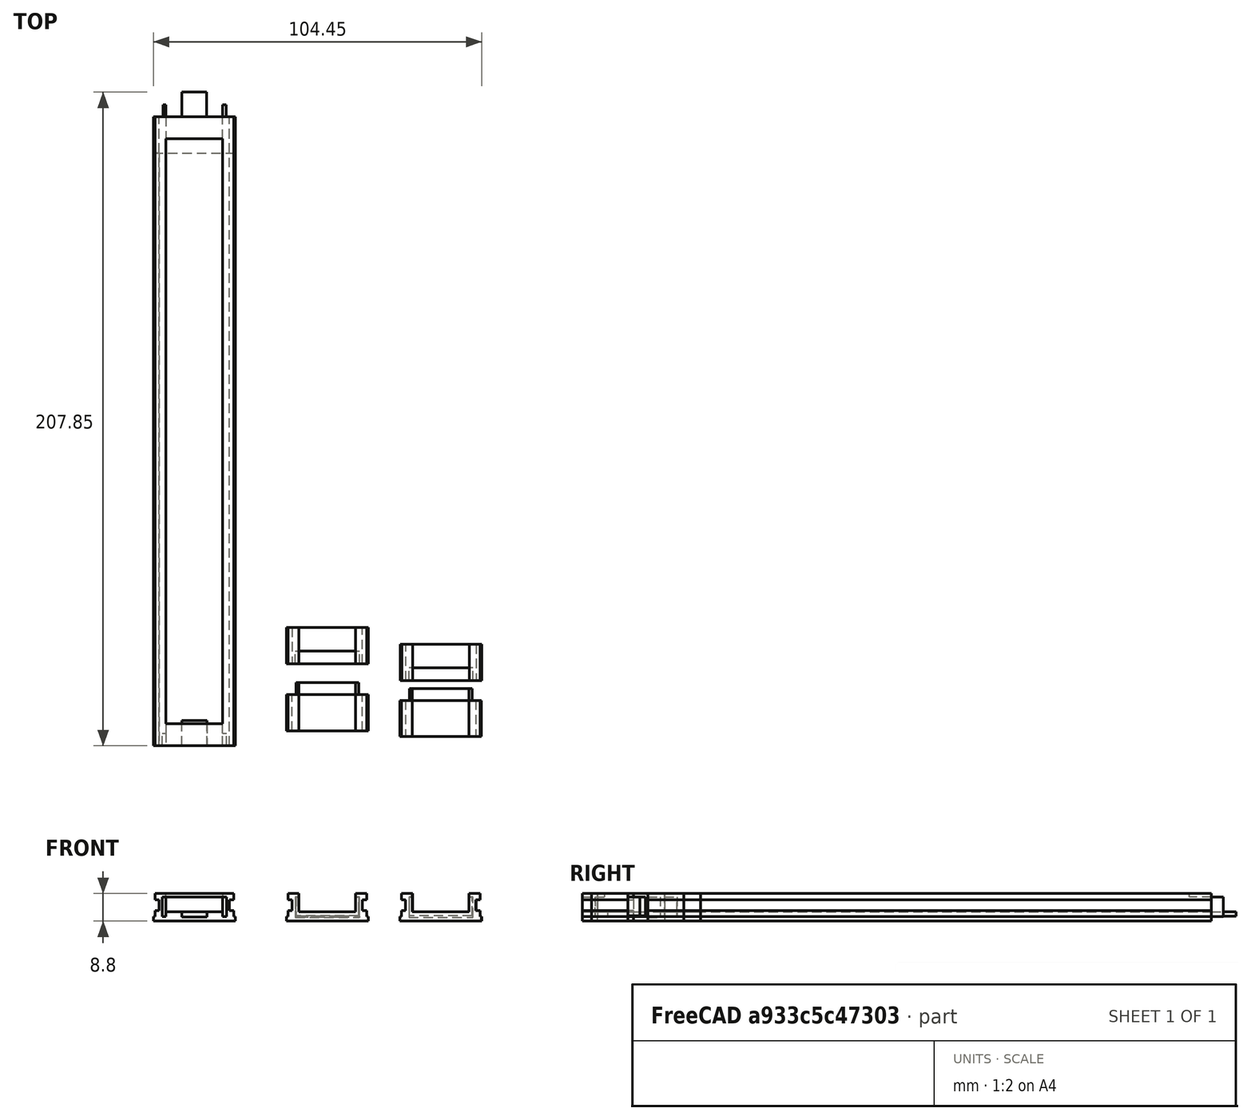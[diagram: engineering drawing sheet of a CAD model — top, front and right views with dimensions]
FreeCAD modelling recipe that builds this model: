
FCSTD DOCUMENT  (FreeCAD 0.18.3R)
Label: lamp.rail.template
License: All rights reserved
LicenseURL: http://en.wikipedia.org/wiki/All_rights_reserved
objects: Part::Extrusion×64, Part::Part2DObjectPython×46, Part::Cut×32, Part::Feature×26, Part::MultiFuse×13, Part::FeaturePython×3
note: 184 computed .brp shape members not serialized (recipe doc carries the construction recipe); baked Part::Feature solids carry a one-line shape summary decoded from their .brp

FEATURE [Part::Part2DObjectPython] Rectangle014  # Draft 2D object (typed FeaturePython)
  ChamferSize = 0
  Columns = 1
  FilletRadius = 0
  Height = 2
  Length = 24
  MakeFace = true
  Placement = pos=(-4.28928,0,-0.735044) rot=(1,0,0;1.5708rad)
  Rows = 1
FEATURE [Part::Part2DObjectPython] Rectangle013  # Draft 2D object (typed FeaturePython)
  ChamferSize = 0
  Columns = 1
  FilletRadius = 0
  Height = 2
  Length = 24
  MakeFace = true
  Placement = pos=(-4.28928,1.2e-15,4.66496) rot=(1,0,0;1.5708rad)
  Rows = 1
  Support = -> [Rectangle014]
FEATURE [Part::Part2DObjectPython] Rectangle015  # Draft 2D object (typed FeaturePython)
  ChamferSize = 0
  Columns = 1
  FilletRadius = 0
  Height = 7.5
  Length = 7.85
  MakeFace = true
  Placement = pos=(3.96072,7.85,0.865504) rot=(0,0,-1;1.5708rad)
  Rows = 1
FEATURE [Part::Part2DObjectPython] Rectangle016  # Draft 2D object (typed FeaturePython)
  ChamferSize = 0
  Columns = 1
  FilletRadius = 0
  Height = 5.79945
  Length = 13
  MakeFace = true
  Placement = pos=(14.2107,0,0.865504) rot=(0,0.707107,0.707107;3.14159rad)
  Rows = 1
FEATURE [Part::Part2DObjectPython] Rectangle017  # Draft 2D object (typed FeaturePython)
  ChamferSize = 0
  Columns = 1
  FilletRadius = 0
  Height = 3.4
  Length = 21.5
  MakeFace = true
  Placement = pos=(-3.03928,0,1.26496) rot=(1,0,0;1.5708rad)
  Rows = 1
  Support = -> [Rectangle013]
FEATURE [Part::Extrusion] Extrude026
  Base = -> Rectangle014
  Dir = (0,-1,2e-16)
  DirMode = 2
  FaceMakerClass = Part::FaceMakerBullseye
  LengthFwd = 23
  LengthRev = 0
  Solid = false
  Symmetric = false
FEATURE [Part::Extrusion] Extrude027
  Base = -> Rectangle016
  Dir = (0,1,-2e-16)
  DirMode = 2
  FaceMakerClass = Part::FaceMakerBullseye
  LengthFwd = -23
  LengthRev = 0
  Solid = false
  Symmetric = false
FEATURE [Part::Extrusion] Extrude028
  Base = -> Rectangle017
  Dir = (0,-1,2e-16)
  DirMode = 2
  FaceMakerClass = Part::FaceMakerBullseye
  LengthFwd = 23
  LengthRev = 0
  Solid = false
  Symmetric = false
FEATURE [Part::Extrusion] Extrude029
  Base = -> Rectangle013
  Dir = (0,-1,2e-16)
  DirMode = 2
  FaceMakerClass = Part::FaceMakerBullseye
  LengthFwd = 23
  LengthRev = 0
  Solid = false
  Symmetric = false
FEATURE [Part::Part2DObjectPython] Rectangle018  # Draft 2D object (typed FeaturePython)
  ChamferSize = 0
  Columns = 1
  FilletRadius = 0
  Height = 1.39945
  Length = 25
  MakeFace = true
  Placement = pos=(20.2107,-1e-15,-2.1345) rot=(0,0.707107,0.707107;3.14159rad)
  Rows = 1
FEATURE [Part::Extrusion] Extrude025
  Base = -> Rectangle018
  Dir = (0,1,-2e-16)
  DirMode = 2
  FaceMakerClass = Part::FaceMakerBullseye
  LengthFwd = -23
  LengthRev = 0
  Solid = false
  Symmetric = false
FEATURE [Part::MultiFuse] Fusion003
  Shapes = -> [Extrude029,Extrude028,Extrude026,Extrude025]
FEATURE [Part::Cut] Cut008
  Base = -> Fusion003
  Tool = -> Extrude027
FEATURE [Part::Part2DObjectPython] Rectangle020  # Draft 2D object (typed FeaturePython)
  ChamferSize = 0
  Columns = 1
  FilletRadius = 0
  Height = 2.5
  Length = 8
  MakeFace = true
  Placement = pos=(3.71072,-23,-1.6345) rot=(1,0,0;1.5708rad)
  Rows = 1
  Support = -> [Cut008]
FEATURE [Part::Extrusion] Extrude030
  Base = -> Rectangle020
  Dir = (-1e-16,-1,2e-16)
  DirMode = 2
  FaceMakerClass = Part::FaceMakerBullseye
  LengthFwd = -8
  LengthRev = 0
  Solid = false
  Symmetric = false
FEATURE [Part::Cut] Cut009
  Base = -> Cut008
  Tool = -> Extrude030
FEATURE [Part::Extrusion] Extrude031
  Base = -> Rectangle015
  Dir = (0,2e-16,1)
  DirMode = 2
  FaceMakerClass = Part::FaceMakerBullseye
  LengthFwd = -2
  LengthRev = 0
  Solid = false
  Symmetric = false
FEATURE [Part::MultiFuse] Fusion002
  Shapes = -> [Cut009,Extrude031]
FEATURE [Part::Part2DObjectPython] Rectangle019  # Draft 2D object (typed FeaturePython)
  ChamferSize = 0
  Columns = 1
  FilletRadius = 0
  Height = 23
  Length = 15
  MakeFace = true
  Placement = pos=(15.2107,0,6.66496) rot=(0,0,1;3.14159rad)
  Rows = 1
  Support = -> [Fusion002]
FEATURE [Part::Extrusion] Extrude024
  Base = -> Rectangle019
  Dir = (0,2e-16,1)
  DirMode = 2
  FaceMakerClass = Part::FaceMakerBullseye
  LengthFwd = -5.8
  LengthRev = 0
  Solid = false
  Symmetric = false
FEATURE [Part::Cut] Cut010
  Base = -> Fusion002
  Placement = pos=(1.15935,45.2064,-9.8e-15) rot=(0,0,1;0rad)
  Tool = -> Extrude024
FEATURE [Part::Part2DObjectPython] Rectangle021  # Draft 2D object (typed FeaturePython)
  ChamferSize = 0
  Columns = 1
  FilletRadius = 0
  Height = 32.5147
  Length = 55.6938
  MakeFace = true
  Placement = pos=(36.717,33.7064,-13.163) rot=(0,0.707107,0.707107;3.14159rad)
  Rows = 1
  Support = -> [Cut010]
FEATURE [Part::FeaturePython] Slice  # WARN: FeaturePython — macro-defined, semantics opaque (R4)
  Base = -> Cut010
  Mode = 1
  Tolerance = 0
  Tools = -> [Rectangle021]
FEATURE [Part::FeaturePython] Slice_child0  label="Slice.0"  # WARN: FeaturePython — macro-defined, semantics opaque (R4)
  Base = -> Slice
  FilterType = 1
  Invert = false
  OverrideMaxVal = 0
  Placement = pos=(-30.6082,-11.7295,9e-16) rot=(0,0,1;0rad)
  WindowFrom = 80
  WindowTo = 100
  items = 0
FEATURE [Part::FeaturePython] Slice_child1  label="Slice.1"  # WARN: FeaturePython — macro-defined, semantics opaque (R4)
  Base = -> Slice
  FilterType = 1
  Invert = false
  OverrideMaxVal = 0
  WindowFrom = 80
  WindowTo = 100
  items = 1
FEATURE [Part::Feature] Face
  Placement = pos=(-29.4488,33.4769,-8.9e-15) rot=(0,0,1;0rad)
  shape: bbox 2e-07 x 7.85 x 2 mm, 1 faces, 0 solids (baked)
FEATURE [Part::Extrusion] Extrusion
  Base = -> Face
  Dir = (0.2,0,0)
  DirMode = 0
  FaceMakerClass = Part::FaceMakerBullseye
  LengthFwd = 0
  LengthRev = 0
  Solid = true
  Symmetric = false
FEATURE [Part::Feature] Face001
  Placement = pos=(-29.4488,33.4769,-8.9e-15) rot=(0,0,1;0rad)
  shape: bbox 2e-07 x 7.85 x 2 mm, 1 faces, 0 solids (baked)
FEATURE [Part::Extrusion] Extrusion001
  Base = -> Face001
  Dir = (-0.2,0,0)
  DirMode = 0
  FaceMakerClass = Part::FaceMakerBullseye
  LengthFwd = 0
  LengthRev = 0
  Solid = true
  Symmetric = false
FEATURE [Part::MultiFuse] Fusion004
  Shapes = -> [Extrusion,Extrusion001,Slice_child0]
FEATURE [Part::Part2DObjectPython] Rectangle024  # Draft 2D object (typed FeaturePython)
  ChamferSize = 0
  Columns = 1
  FilletRadius = 0
  Height = 17
  Length = 11.5
  MakeFace = true
  Placement = pos=(-30.2381,33.4769,0.864956) rot=(0,0,-1;1.5708rad)
  Rows = 1
  Support = -> [Slice_child1]
FEATURE [Part::Extrusion] Extrude032
  Base = -> Rectangle024
  Dir = (0,2e-16,1)
  DirMode = 2
  FaceMakerClass = Part::FaceMakerBullseye
  LengthFwd = 10
  LengthRev = 0
  Solid = false
  Symmetric = false
FEATURE [Part::Cut] Cut011
  Base = -> Fusion004
  Tool = -> Extrude032
FEATURE [Part::Part2DObjectPython] Rectangle025  # Draft 2D object (typed FeaturePython)
  ChamferSize = 0
  Columns = 1
  FilletRadius = 0
  Height = 17
  Length = 11.5
  MakeFace = true
  Placement = pos=(0.370074,33.7064,0.864956) rot=(0,0,-1;1.5708rad)
  Rows = 1
FEATURE [Part::Extrusion] Extrude033
  Base = -> Rectangle025
  Dir = (0,2e-16,1)
  DirMode = 2
  FaceMakerClass = Part::FaceMakerBullseye
  LengthFwd = 10
  LengthRev = 0
  Solid = false
  Symmetric = false
FEATURE [Part::Cut] Cut012
  Base = -> Slice_child1
  Tool = -> Extrude033
FEATURE [Part::Part2DObjectPython] Rectangle027  # Draft 2D object (typed FeaturePython)
  ChamferSize = 0
  Columns = 1
  FilletRadius = 0
  Height = 3.8
  Length = 8
  MakeFace = true
  Placement = pos=(4.87007,22.2064,-1.6345) rot=(0,0,1;0rad)
  Rows = 1
  Support = -> [Cut012]
FEATURE [Part::Part2DObjectPython] Rectangle028  # Draft 2D object (typed FeaturePython)
  ChamferSize = 0
  Columns = 1
  FilletRadius = 0
  Height = 4
  Length = 7.9
  MakeFace = true
  Placement = pos=(-25.6881,33.4769,-1.1345) rot=(0,0,1;0rad)
  Rows = 1
FEATURE [Part::Extrusion] Extrude040
  Base = -> Rectangle028
  Dir = (0,2e-16,1)
  DirMode = 2
  FaceMakerClass = Part::FaceMakerBullseye
  LengthFwd = 0.6
  LengthRev = 0
  Solid = false
  Symmetric = false
FEATURE [Part::Cut] Cut018
  Base = -> Cut011
  Tool = -> Extrude040
FEATURE [Part::Extrusion] Extrude041
  Base = -> Rectangle027
  Dir = (0,2e-16,1)
  DirMode = 2
  FaceMakerClass = Part::FaceMakerBullseye
  LengthFwd = 0.9
  LengthRev = 0
  Solid = false
  Symmetric = false
FEATURE [Part::MultiFuse] Fusion005
  Shapes = -> [Cut012,Extrude041]
FEATURE [Part::Part2DObjectPython] Rectangle029  # Draft 2D object (typed FeaturePython)
  ChamferSize = 0
  Columns = 1
  FilletRadius = 0
  Height = 3.85
  Length = 7.9
  MakeFace = true
  Placement = pos=(-17.7881,37.4769,-1.1345) rot=(0,1,0;3.14159rad)
  Rows = 1
  Support = -> [Cut018]
FEATURE [Part::Extrusion] Extrude042
  Base = -> Rectangle029
  Dir = (0,0,-1)
  DirMode = 2
  FaceMakerClass = Part::FaceMakerBullseye
  LengthFwd = 0.1
  LengthRev = 0
  Solid = false
  Symmetric = false
FEATURE [Part::MultiFuse] Fusion006
  Shapes = -> [Cut018,Extrude042]
FEATURE [Part::Part2DObjectPython] Rectangle030  # Draft 2D object (typed FeaturePython)
  ChamferSize = 0
  Columns = 1
  FilletRadius = 0
  Height = 6.3
  Length = 1.1
  MakeFace = true
  Placement = pos=(-12.1381,33.4769,-0.735044) rot=(0,0.707107,0.707107;3.14159rad)
  Rows = 1
  Support = -> [Fusion006]
FEATURE [Part::Part2DObjectPython] Rectangle031  # Draft 2D object (typed FeaturePython)
  ChamferSize = 0
  Columns = 1
  FilletRadius = 0
  Height = 6.3
  Length = 1
  MakeFace = true
  Placement = pos=(-30.2381,33.4769,-0.735044) rot=(0,0.707107,0.707107;3.14159rad)
  Rows = 1
FEATURE [Part::Part2DObjectPython] Rectangle032  # Draft 2D object (typed FeaturePython)
  ChamferSize = 0
  Columns = 1
  FilletRadius = 0
  Height = 6.3
  Length = 1.2
  MakeFace = true
  Placement = pos=(-0.829926,22.2064,-0.735044) rot=(1,0,0;1.5708rad)
  Rows = 1
  Support = -> [Fusion005]
FEATURE [Part::Part2DObjectPython] Rectangle033  # Draft 2D object (typed FeaturePython)
  ChamferSize = 0
  Columns = 1
  FilletRadius = 0
  Height = 6.3
  Length = 1.2
  MakeFace = true
  Placement = pos=(17.3701,22.2064,-0.735044) rot=(1,0,0;1.5708rad)
  Rows = 1
FEATURE [Part::Extrusion] Extrude045
  Base = -> Rectangle032
  Dir = (2.69e-14,-1,2e-16)
  DirMode = 2
  FaceMakerClass = Part::FaceMakerBullseye
  LengthFwd = -4
  LengthRev = 0
  Placement = pos=(-0.5,-1.14e-13,0) rot=(0,0,1;0rad)
  Solid = false
  Symmetric = false
FEATURE [Part::Extrusion] Extrude046
  Base = -> Rectangle033
  Dir = (2.69e-14,-1,2e-16)
  DirMode = 2
  FaceMakerClass = Part::FaceMakerBullseye
  LengthFwd = -4
  LengthRev = 0
  Placement = pos=(0.5,1.101e-13,0) rot=(0,0,1;0rad)
  Solid = false
  Symmetric = false
FEATURE [Part::Extrusion] Extrude047
  Base = -> Rectangle030
  Dir = (-2.5e-14,1,-2e-16)
  DirMode = 2
  FaceMakerClass = Part::FaceMakerBullseye
  LengthFwd = 3.8
  LengthRev = 0
  Solid = false
  Symmetric = false
FEATURE [Part::Extrusion] Extrude048
  Base = -> Rectangle031
  Dir = (-2.5e-14,1,-2e-16)
  DirMode = 2
  FaceMakerClass = Part::FaceMakerBullseye
  LengthFwd = 3.8
  LengthRev = 0
  Solid = false
  Symmetric = false
FEATURE [Part::Part2DObjectPython] Rectangle034  # Draft 2D object (typed FeaturePython)
  ChamferSize = 0
  Columns = 1
  FilletRadius = 0
  Height = 3.8
  Length = 1.1
  MakeFace = true
  Placement = pos=(-12.1381,33.4769,-0.735044) rot=(0,1,0;3.14159rad)
  Rows = 1
  Support = -> [Extrude047]
FEATURE [Part::Extrusion] Extrude049
  Base = -> Rectangle034
  Dir = (2.55e-14,-2e-16,-1)
  DirMode = 2
  FaceMakerClass = Part::FaceMakerBullseye
  LengthFwd = -0.1
  LengthRev = 0
  Solid = false
  Symmetric = false
FEATURE [Part::Cut] Cut021
  Base = -> Extrude047
  Placement = pos=(0.5,2.27e-13,0) rot=(0,0,1;0rad)
  Tool = -> Extrude049
FEATURE [Part::Part2DObjectPython] Rectangle035  # Draft 2D object (typed FeaturePython)
  ChamferSize = 0
  Columns = 1
  FilletRadius = 0
  Height = 3.8
  Length = 1
  MakeFace = true
  Placement = pos=(-30.2381,33.4769,-0.735044) rot=(0,1,0;3.14159rad)
  Rows = 1
  Support = -> [Fusion006]
FEATURE [Part::Extrusion] Extrude050
  Base = -> Rectangle035
  Dir = (2.55e-14,-2e-16,-1)
  DirMode = 2
  FaceMakerClass = Part::FaceMakerBullseye
  LengthFwd = -0.1
  LengthRev = 0
  Solid = false
  Symmetric = false
FEATURE [Part::Cut] Cut022
  Base = -> Extrude048
  Placement = pos=(-0.5,-7.1e-15,0) rot=(0,0,1;0rad)
  Tool = -> Extrude050
FEATURE [Part::Part2DObjectPython] Rectangle036  # Draft 2D object (typed FeaturePython)
  ChamferSize = 0
  Columns = 1
  FilletRadius = 0
  Height = 3.85
  Length = 7.9
  MakeFace = true
  Placement = pos=(-17.7881,37.4769,-1.2345) rot=(0,1,0;3.14159rad)
  Rows = 1
FEATURE [Part::Extrusion] Extrude051
  Base = -> Rectangle036
  Dir = (0,0,-1)
  DirMode = 2
  FaceMakerClass = Part::FaceMakerBullseye
  LengthFwd = 0.1
  LengthRev = 0
  Solid = false
  Symmetric = false
FEATURE [Part::Part2DObjectPython] Rectangle037  # Draft 2D object (typed FeaturePython)
  ChamferSize = 0
  Columns = 1
  FilletRadius = 0
  Height = 7.9
  Length = 4.1
  MakeFace = true
  Placement = pos=(-25.6881,33.4769,-0.534496) rot=(0.707107,0.707107,0;3.14159rad)
  Rows = 1
FEATURE [Part::Extrusion] Extrude052
  Base = -> Rectangle037
  Dir = (0,-3e-16,-1)
  DirMode = 2
  FaceMakerClass = Part::FaceMakerBullseye
  LengthFwd = 1
  LengthRev = 0
  Solid = false
  Symmetric = false
FEATURE [Part::Part2DObjectPython] Rectangle038  # Draft 2D object (typed FeaturePython)
  ChamferSize = 0
  Columns = 1
  FilletRadius = 0
  Height = 3.8
  Length = 8
  MakeFace = true
  Placement = pos=(4.87007,22.2064,-0.734496) rot=(0,0,1;0rad)
  Rows = 1
FEATURE [Part::Extrusion] Extrude053
  Base = -> Rectangle038
  Dir = (0,2e-16,1)
  DirMode = 2
  FaceMakerClass = Part::FaceMakerBullseye
  LengthFwd = -0.1
  LengthRev = 0
  Solid = false
  Symmetric = false
FEATURE [Part::Part2DObjectPython] Rectangle039  # Draft 2D object (typed FeaturePython)
  ChamferSize = 0
  Columns = 1
  FilletRadius = 0
  Height = 2
  Length = 11.5
  MakeFace = true
  Placement = pos=(-33.7381,33.4769,4.66496) rot=(0.57735,-0.57735,-0.57735;2.0944rad)
  Rows = 1
FEATURE [Part::Extrusion] Extrude054
  Base = -> Rectangle039
  Dir = (-1,-2e-16,-2e-16)
  DirMode = 2
  FaceMakerClass = Part::FaceMakerBullseye
  LengthFwd = 0.5
  LengthRev = 0
  Solid = false
  Symmetric = false
FEATURE [Part::Part2DObjectPython] Rectangle040  # Draft 2D object (typed FeaturePython)
  ChamferSize = 0
  Columns = 1
  FilletRadius = 0
  Height = 2
  Length = 11.5
  MakeFace = true
  Placement = pos=(-33.7381,33.4769,-0.735044) rot=(0.57735,-0.57735,-0.57735;2.0944rad)
  Rows = 1
FEATURE [Part::Extrusion] Extrude055
  Base = -> Rectangle040
  Dir = (-1,-2e-16,-2e-16)
  DirMode = 2
  FaceMakerClass = Part::FaceMakerBullseye
  LengthFwd = 0.5
  LengthRev = 0
  Solid = false
  Symmetric = false
FEATURE [Part::Part2DObjectPython] Rectangle041  # Draft 2D object (typed FeaturePython)
  ChamferSize = 0
  Columns = 1
  FilletRadius = 0
  Height = 1.39945
  Length = 11.5
  MakeFace = true
  Placement = pos=(-34.2381,33.4769,-2.1345) rot=(0.57735,-0.57735,-0.57735;2.0944rad)
  Rows = 1
FEATURE [Part::Extrusion] Extrude056
  Base = -> Rectangle041
  Dir = (-1,-2e-16,-2e-16)
  DirMode = 2
  FaceMakerClass = Part::FaceMakerBullseye
  LengthFwd = 0.5
  LengthRev = 0
  Solid = false
  Symmetric = false
FEATURE [Part::Part2DObjectPython] Rectangle042  # Draft 2D object (typed FeaturePython)
  ChamferSize = 0
  Columns = 1
  FilletRadius = 0
  Height = 3.4
  Length = 11.5
  MakeFace = true
  Placement = pos=(-32.4881,33.4769,1.26496) rot=(0.57735,-0.57735,-0.57735;2.0944rad)
  Rows = 1
FEATURE [Part::Extrusion] Extrude057
  Base = -> Rectangle042
  Dir = (-1,-2e-16,-2e-16)
  DirMode = 2
  FaceMakerClass = Part::FaceMakerBullseye
  LengthFwd = 0.4
  LengthRev = 0
  Solid = false
  Symmetric = false
FEATURE [Part::Part2DObjectPython] Rectangle043  # Draft 2D object (typed FeaturePython)
  ChamferSize = 0
  Columns = 1
  FilletRadius = 0
  Height = 3.4
  Length = 11.5
  MakeFace = true
  Placement = pos=(-10.9881,33.4769,1.26496) rot=(0.57735,-0.57735,-0.57735;2.0944rad)
  Rows = 1
FEATURE [Part::Extrusion] Extrude058
  Base = -> Rectangle043
  Dir = (-1,-2e-16,-2e-16)
  DirMode = 2
  FaceMakerClass = Part::FaceMakerBullseye
  LengthFwd = -0.4
  LengthRev = 0
  Solid = false
  Symmetric = false
FEATURE [Part::Part2DObjectPython] Rectangle044  # Draft 2D object (typed FeaturePython)
  ChamferSize = 0
  Columns = 1
  FilletRadius = 0
  Height = 2
  Length = 11.5
  MakeFace = true
  Placement = pos=(-9.73812,33.4769,4.66496) rot=(0.57735,-0.57735,-0.57735;2.0944rad)
  Rows = 1
FEATURE [Part::Part2DObjectPython] Rectangle045  # Draft 2D object (typed FeaturePython)
  ChamferSize = 0
  Columns = 1
  FilletRadius = 0
  Height = 2
  Length = 11.5
  MakeFace = true
  Placement = pos=(-9.73812,33.4769,-0.735044) rot=(0.57735,-0.57735,-0.57735;2.0944rad)
  Rows = 1
FEATURE [Part::Part2DObjectPython] Rectangle046  # Draft 2D object (typed FeaturePython)
  ChamferSize = 0
  Columns = 1
  FilletRadius = 0
  Height = 1.39945
  Length = 11.5
  MakeFace = true
  Placement = pos=(-9.23812,33.4769,-2.1345) rot=(0.57735,-0.57735,-0.57735;2.0944rad)
  Rows = 1
FEATURE [Part::Extrusion] Extrude059
  Base = -> Rectangle044
  Dir = (-1,-2e-16,-2e-16)
  DirMode = 2
  FaceMakerClass = Part::FaceMakerBullseye
  LengthFwd = -0.5
  LengthRev = 0
  Solid = false
  Symmetric = false
FEATURE [Part::Extrusion] Extrude060
  Base = -> Rectangle045
  Dir = (-1,-2e-16,-2e-16)
  DirMode = 2
  FaceMakerClass = Part::FaceMakerBullseye
  LengthFwd = -0.5
  LengthRev = 0
  Solid = false
  Symmetric = false
FEATURE [Part::Extrusion] Extrude061
  Base = -> Rectangle046
  Dir = (-1,-2e-16,-2e-16)
  DirMode = 2
  FaceMakerClass = Part::FaceMakerBullseye
  LengthFwd = -0.5
  LengthRev = 0
  Solid = false
  Symmetric = false
FEATURE [Part::Part2DObjectPython] Rectangle047  # Draft 2D object (typed FeaturePython)
  ChamferSize = 0
  Columns = 1
  FilletRadius = 0
  Height = 11.5
  Length = 18
  MakeFace = true
  Placement = pos=(-30.7381,21.9769,0.864956) rot=(0,0,1;0rad)
  Rows = 1
FEATURE [Part::Extrusion] Extrude062
  Base = -> Rectangle047
  Dir = (0,0,1)
  DirMode = 2
  FaceMakerClass = Part::FaceMakerBullseye
  LengthFwd = 10
  LengthRev = 0
  Solid = false
  Symmetric = false
FEATURE [Part::Cut] Cut025
  Base = -> Fusion006
  Tool = -> Extrude062
FEATURE [Part::MultiFuse] Fusion007
  Shapes = -> [Extrude051,Cut025]
FEATURE [Part::Cut] Cut026
  Base = -> Fusion007
  Tool = -> Extrude052
FEATURE [Part::MultiFuse] Fusion008
  Shapes = -> [Cut026,Extrude061,Extrude060,Extrude058,Extrude059,Extrude056,Extrude055,Extrude057,Extrude054]
FEATURE [Part::Part2DObjectPython] Rectangle048  # Draft 2D object (typed FeaturePython)
  ChamferSize = 0
  Columns = 1
  FilletRadius = 0
  Height = 2
  Length = 11.5
  MakeFace = true
  Placement = pos=(20.8701,33.7064,6.66496) rot=(0.57735,-0.57735,0.57735;4.18879rad)
  Rows = 1
FEATURE [Part::Part2DObjectPython] Rectangle049  # Draft 2D object (typed FeaturePython)
  ChamferSize = 0
  Columns = 1
  FilletRadius = 0
  Height = 2
  Length = 11.5
  MakeFace = true
  Placement = pos=(20.8701,33.7064,1.26496) rot=(0.57735,-0.57735,0.57735;4.18879rad)
  Rows = 1
FEATURE [Part::Part2DObjectPython] Rectangle050  # Draft 2D object (typed FeaturePython)
  ChamferSize = 0
  Columns = 1
  FilletRadius = 0
  Height = 1.39945
  Length = 11.5
  MakeFace = true
  Placement = pos=(21.3701,33.7064,-0.735044) rot=(0.57735,-0.57735,0.57735;4.18879rad)
  Rows = 1
FEATURE [Part::Part2DObjectPython] Rectangle051  # Draft 2D object (typed FeaturePython)
  ChamferSize = 0
  Columns = 1
  FilletRadius = 0
  Height = 3.4
  Length = 11.5
  MakeFace = true
  Placement = pos=(19.6201,33.7064,4.66496) rot=(0.57735,-0.57735,0.57735;4.18879rad)
  Rows = 1
FEATURE [Part::Part2DObjectPython] Rectangle052  # Draft 2D object (typed FeaturePython)
  ChamferSize = 0
  Columns = 1
  FilletRadius = 0
  Height = 2
  Length = 11.5
  MakeFace = true
  Placement = pos=(-3.12993,33.7064,6.66496) rot=(0.57735,-0.57735,0.57735;4.18879rad)
  Rows = 1
FEATURE [Part::Part2DObjectPython] Rectangle053  # Draft 2D object (typed FeaturePython)
  ChamferSize = 0
  Columns = 1
  FilletRadius = 0
  Height = 3.4
  Length = 11.5
  MakeFace = true
  Placement = pos=(-1.87993,33.7064,4.66496) rot=(0.57735,-0.57735,0.57735;4.18879rad)
  Rows = 1
FEATURE [Part::Part2DObjectPython] Rectangle054  # Draft 2D object (typed FeaturePython)
  ChamferSize = 0
  Columns = 1
  FilletRadius = 0
  Height = 2
  Length = 11.5
  MakeFace = true
  Placement = pos=(-3.12993,33.7064,1.26496) rot=(0.57735,-0.57735,0.57735;4.18879rad)
  Rows = 1
FEATURE [Part::Part2DObjectPython] Rectangle055  # Draft 2D object (typed FeaturePython)
  ChamferSize = 0
  Columns = 1
  FilletRadius = 0
  Height = 1.39945
  Length = 11.5
  MakeFace = true
  Placement = pos=(-3.62993,33.7064,-0.735044) rot=(0.57735,-0.57735,0.57735;4.18879rad)
  Rows = 1
FEATURE [Part::Extrusion] Extrude063
  Base = -> Rectangle048
  Dir = (1,-1e-16,1e-16)
  DirMode = 2
  FaceMakerClass = Part::FaceMakerBullseye
  LengthFwd = 0.5
  LengthRev = 0
  Solid = false
  Symmetric = false
FEATURE [Part::Extrusion] Extrude064
  Base = -> Rectangle049
  Dir = (1,-1e-16,1e-16)
  DirMode = 2
  FaceMakerClass = Part::FaceMakerBullseye
  LengthFwd = 0.5
  LengthRev = 0
  Solid = false
  Symmetric = false
FEATURE [Part::Extrusion] Extrude065
  Base = -> Rectangle050
  Dir = (1,-1e-16,1e-16)
  DirMode = 2
  FaceMakerClass = Part::FaceMakerBullseye
  LengthFwd = 0.5
  LengthRev = 0
  Solid = false
  Symmetric = false
FEATURE [Part::Extrusion] Extrude066
  Base = -> Rectangle052
  Dir = (1,-1e-16,1e-16)
  DirMode = 2
  FaceMakerClass = Part::FaceMakerBullseye
  LengthFwd = -0.5
  LengthRev = 0
  Solid = false
  Symmetric = false
FEATURE [Part::Extrusion] Extrude067
  Base = -> Rectangle054
  Dir = (1,-1e-16,1e-16)
  DirMode = 2
  FaceMakerClass = Part::FaceMakerBullseye
  LengthFwd = -0.5
  LengthRev = 0
  Solid = false
  Symmetric = false
FEATURE [Part::Extrusion] Extrude068
  Base = -> Rectangle055
  Dir = (1,-1e-16,1e-16)
  DirMode = 2
  FaceMakerClass = Part::FaceMakerBullseye
  LengthFwd = -0.5
  LengthRev = 0
  Solid = false
  Symmetric = false
FEATURE [Part::Extrusion] Extrude069
  Base = -> Rectangle053
  Dir = (1,-1e-16,1e-16)
  DirMode = 2
  FaceMakerClass = Part::FaceMakerBullseye
  LengthFwd = -0.4
  LengthRev = 0
  Solid = false
  Symmetric = false
FEATURE [Part::Part2DObjectPython] Rectangle056  # Draft 2D object (typed FeaturePython)
  ChamferSize = 0
  Columns = 1
  FilletRadius = 0
  Height = 11.5
  Length = 18
  MakeFace = true
  Placement = pos=(-0.129926,22.2064,0.864956) rot=(0,0,1;0rad)
  Rows = 1
  Support = -> [Fusion005]
FEATURE [Part::Extrusion] Extrude070
  Base = -> Rectangle056
  Dir = (0,0,1)
  DirMode = 2
  FaceMakerClass = Part::FaceMakerBullseye
  LengthFwd = 10
  LengthRev = 0
  Solid = false
  Symmetric = false
FEATURE [Part::Cut] Cut027
  Base = -> Fusion005
  Tool = -> Extrude070
FEATURE [Part::Cut] Cut028
  Base = -> Cut027
  Tool = -> Extrude045
FEATURE [Part::Cut] Cut029
  Base = -> Cut028
  Tool = -> Extrude046
FEATURE [Part::Extrusion] Extrude071
  Base = -> Rectangle051
  Dir = (1,-1e-16,1e-16)
  DirMode = 2
  FaceMakerClass = Part::FaceMakerBullseye
  LengthFwd = 0.4
  LengthRev = 0
  Solid = false
  Symmetric = false
FEATURE [Part::MultiFuse] Fusion010
  Shapes = -> [Extrude063,Extrude064,Extrude065,Extrude066,Extrude067,Extrude068,Extrude069,Extrude071]
FEATURE [Part::Cut] Cut030
  Base = -> Cut029
  Tool = -> Extrude053
FEATURE [Part::MultiFuse] Fusion011
  Placement = pos=(-30.6082,21.1066,-8e-15) rot=(0,0,1;0rad)
  Shapes = -> [Cut030,Fusion010]
FEATURE [Part::MultiFuse] Fusion012
  Shapes = -> [Cut021,Cut022,Fusion008]
FEATURE [Part::Part2DObjectPython] Rectangle057  # Draft 2D object (typed FeaturePython)
  ChamferSize = 0
  Columns = 1
  FilletRadius = 0
  Height = 3.75
  Length = 7.9
  MakeFace = true
  Placement = pos=(-25.6881,41.3269,-1.3345) rot=(1,0,0;3.14159rad)
  Rows = 1
  Support = -> [Fusion012]
FEATURE [Part::Extrusion] Extrude072
  Base = -> Rectangle057
  Dir = (0,-1e-16,-1)
  DirMode = 2
  FaceMakerClass = Part::FaceMakerBullseye
  LengthFwd = -0.8
  LengthRev = 0
  Solid = false
  Symmetric = false
FEATURE [Part::Cut] Cut031
  Base = -> Fusion012
  Tool = -> Extrude072
FEATURE [Part::Feature] Face002
  Placement = pos=(-30.6082,21.1066,-8e-15) rot=(0,0,1;0rad)
  shape: bbox 8 x 4.2 x 3e-07 mm, 1 faces, 0 solids (baked)
FEATURE [Part::Extrusion] Extrusion002
  Base = -> Face002
  Dir = (0,2e-16,0.8)
  DirMode = 0
  FaceMakerClass = Part::FaceMakerBullseye
  LengthFwd = 0
  LengthRev = 0
  Solid = true
  Symmetric = false
FEATURE [Part::MultiFuse] Fusion
  Shapes = -> [Extrusion002,Fusion011]
FEATURE [Part::Feature] Fusion013005001  label="Fusion013006"
  shape: bbox 26 x 207.9 x 8.8 mm, 55 faces (baked)
FEATURE [Part::Feature] Face003
  Placement = pos=(-30.6082,21.1066,-8e-15) rot=(0,0,1;0rad)
  shape: bbox 5 x 5.243e-07 x 1.6 mm, 1 faces, 0 solids (baked)
FEATURE [Part::Extrusion] Extrusion003
  Base = -> Face003
  Dir = (0,4,0)
  DirMode = 0
  FaceMakerClass = Part::FaceMakerBullseye
  LengthFwd = 0
  LengthRev = 0
  Solid = true
  Symmetric = false
FEATURE [Part::Cut] Cut
  Base = -> Fusion
  Tool = -> Extrusion003
FEATURE [Part::Feature] Face004
  Placement = pos=(-30.6082,21.1066,-8e-15) rot=(0,0,1;0rad)
  shape: bbox 5 x 5.243e-07 x 1.6 mm, 1 faces, 0 solids (baked)
FEATURE [Part::Feature] Face005
  shape: bbox 8 x 5.243e-07 x 1.699 mm, 1 faces, 0 solids (baked)
FEATURE [Part::Extrusion] Extrusion004
  Base = -> Face004
  Dir = (0,4,0)
  DirMode = 0
  FaceMakerClass = Part::FaceMakerBullseye
  LengthFwd = 0
  LengthRev = 0
  Solid = true
  Symmetric = false
FEATURE [Part::Cut] Cut032
  Base = -> Cut
  Tool = -> Extrusion004
FEATURE [Part::Extrusion] Extrusion005
  Base = -> Face005
  Dir = (0,-4,0)
  DirMode = 0
  FaceMakerClass = Part::FaceMakerBullseye
  LengthFwd = 0
  LengthRev = 0
  Solid = true
  Symmetric = false
FEATURE [Part::Feature] Face006
  shape: bbox 5 x 4 x 5.243e-07 mm, 1 faces, 0 solids (baked)
FEATURE [Part::Extrusion] Extrusion006
  Base = -> Face006
  Dir = (0,0,-0.0994518)
  DirMode = 0
  FaceMakerClass = Part::FaceMakerBullseye
  LengthFwd = 0
  LengthRev = 0
  Solid = true
  Symmetric = false
FEATURE [Part::Feature] Face007
  shape: bbox 5 x 4 x 5.243e-07 mm, 1 faces, 0 solids (baked)
FEATURE [Part::Extrusion] Extrusion007
  Base = -> Face007
  Dir = (0,0,-0.0994518)
  DirMode = 0
  FaceMakerClass = Part::FaceMakerBullseye
  LengthFwd = 0
  LengthRev = 0
  Solid = true
  Symmetric = false
FEATURE [Part::Feature] Face008
  shape: bbox 1.2 x 4 x 5.243e-07 mm, 1 faces, 0 solids (baked)
FEATURE [Part::Extrusion] Extrusion008
  Base = -> Face008
  Dir = (2.7e-15,0,-0.0994518)
  DirMode = 0
  FaceMakerClass = Part::FaceMakerBullseye
  LengthFwd = 0
  LengthRev = 0
  Solid = true
  Symmetric = false
FEATURE [Part::Feature] Face009
  shape: bbox 1.2 x 4 x 5.243e-07 mm, 1 faces, 0 solids (baked)
FEATURE [Part::Extrusion] Extrusion009
  Base = -> Face009
  Dir = (2.7e-15,0,-0.0994518)
  DirMode = 0
  FaceMakerClass = Part::FaceMakerBullseye
  LengthFwd = 0
  LengthRev = 0
  Solid = true
  Symmetric = false
FEATURE [Part::Cut] Cut033
  Base = -> Cut032
  Tool = -> Extrusion009
FEATURE [Part::Cut] Cut034
  Base = -> Cut033
  Tool = -> Extrusion008
FEATURE [Part::Cut] Cut035
  Base = -> Cut034
  Tool = -> Extrusion007
FEATURE [Part::Cut] Cut036
  Base = -> Cut035
  Tool = -> Extrusion006
FEATURE [Part::MultiFuse] Fusion013005002
  Shapes = -> [Extrusion005,Cut036]
FEATURE [Part::Feature] Fusion013005002001  label="Fusion013005003"
  shape: bbox 26 x 11.5 x 8.799 mm, 28 faces (baked)
FEATURE [Part::Part2DObjectPython] Rectangle  # Draft 2D object (typed FeaturePython)
  ChamferSize = 0
  Columns = 1
  FilletRadius = 0
  Height = 4
  Length = 20.4
  MakeFace = true
  Placement = pos=(-31.9381,43.313,-0.834496) rot=(0,0,1;0rad)
  Rows = 1
FEATURE [Part::Extrusion] Extrude
  Base = -> Rectangle
  Dir = (-7.3e-15,3e-16,1)
  DirMode = 2
  FaceMakerClass = Part::FaceMakerBullseye
  LengthFwd = -0.1
  LengthRev = 0
  Solid = false
  Symmetric = false
FEATURE [Part::Cut] Cut037
  Base = -> Fusion013005002001
  Tool = -> Extrude
FEATURE [Part::Feature] Cut037_solid  label="Cut037 (Solid)"
  shape: bbox 26 x 11.5 x 8.799 mm, 31 faces (baked)
FEATURE [Part::Feature] Cut037_solid001  label="Cut037 (Solid)001"
  shape: bbox 26 x 11.5 x 8.799 mm, 28 faces (baked)
FEATURE [Part::Feature] Cut037_solid001001  label="Cut037 (Solid)002"
  Placement = pos=(36.1596,-5.32723,-2.2e-15) rot=(0,0,1;0rad)
  shape: bbox 26 x 11.5 x 8.799 mm, 28 faces (baked)
FEATURE [Part::Feature] Face010
  shape: bbox 5.243e-07 x 7.85 x 1.4 mm, 1 faces, 0 solids (baked)
FEATURE [Part::Extrusion] Extrusion010
  Base = -> Face010
  Dir = (-6.05,-1.3e-15,-2e-16)
  DirMode = 0
  FaceMakerClass = Part::FaceMakerBullseye
  LengthFwd = 0
  LengthRev = 0
  Solid = true
  Symmetric = false
FEATURE [Part::Feature] Face011
  shape: bbox 5.243e-07 x 7.85 x 1.4 mm, 1 faces, 0 solids (baked)
FEATURE [Part::Extrusion] Extrusion011
  Base = -> Face011
  Dir = (6.15,1.4e-15,2e-16)
  DirMode = 0
  FaceMakerClass = Part::FaceMakerBullseye
  LengthFwd = 0
  LengthRev = 0
  Solid = true
  Symmetric = false
FEATURE [Part::MultiFuse] Fusion013005002002
  Shapes = -> [Extrusion011,Cut031,Extrusion010]
FEATURE [Part::Feature] Face012
  shape: bbox 6.15 x 5.243e-07 x 1.4 mm, 1 faces, 0 solids (baked)
FEATURE [Part::Extrusion] Extrusion012
  Base = -> Face012
  Dir = (9e-16,-4.05,9e-16)
  DirMode = 0
  FaceMakerClass = Part::FaceMakerBullseye
  LengthFwd = 0
  LengthRev = 0
  Solid = true
  Symmetric = false
FEATURE [Part::Feature] Face013
  shape: bbox 7.5 x 4.243e-07 x 1.4 mm, 1 faces, 0 solids (baked)
FEATURE [Part::Extrusion] Extrusion013
  Base = -> Face013
  Dir = (9e-16,-4.05,9e-16)
  DirMode = 0
  FaceMakerClass = Part::FaceMakerBullseye
  LengthFwd = 0
  LengthRev = 0
  Solid = true
  Symmetric = false
FEATURE [Part::Feature] Face014
  shape: bbox 6.05 x 5.243e-07 x 1.4 mm, 1 faces, 0 solids (baked)
FEATURE [Part::Extrusion] Extrusion014
  Base = -> Face014
  Dir = (9e-16,-4.05,9e-16)
  DirMode = 0
  FaceMakerClass = Part::FaceMakerBullseye
  LengthFwd = 0
  LengthRev = 0
  Solid = true
  Symmetric = false
FEATURE [Part::Feature] Face015
  shape: bbox 0.2 x 4.243e-07 x 1.4 mm, 1 faces, 0 solids (baked)
FEATURE [Part::Extrusion] Extrusion015
  Base = -> Face015
  Dir = (0,-4.05,9e-16)
  DirMode = 0
  FaceMakerClass = Part::FaceMakerBullseye
  LengthFwd = 0
  LengthRev = 0
  Solid = true
  Symmetric = false
FEATURE [Part::Feature] Face016
  shape: bbox 0.2 x 4.243e-07 x 1.4 mm, 1 faces, 0 solids (baked)
FEATURE [Part::Extrusion] Extrusion016
  Base = -> Face016
  Dir = (0,-4.05,9e-16)
  DirMode = 0
  FaceMakerClass = Part::FaceMakerBullseye
  LengthFwd = 0
  LengthRev = 0
  Solid = true
  Symmetric = false
FEATURE [Part::Feature] Face017
  Placement = pos=(-11.6381,33.4769,-0.635044) rot=(0,1,0;3.14159rad)
  shape: bbox 1.1 x 3.8 x 5.243e-07 mm, 1 faces, 0 solids (baked)
FEATURE [Part::Extrusion] Extrusion017
  Base = -> Face017
  Dir = (-2.6e-15,0,0.100548)
  DirMode = 0
  FaceMakerClass = Part::FaceMakerBullseye
  LengthFwd = 0
  LengthRev = 0
  Solid = true
  Symmetric = false
FEATURE [Part::Feature] Face018
  Placement = pos=(-30.7381,33.4769,-0.635044) rot=(0,1,0;3.14159rad)
  shape: bbox 1 x 3.8 x 5.243e-07 mm, 1 faces, 0 solids (baked)
FEATURE [Part::Extrusion] Extrusion018
  Base = -> Face018
  Dir = (-2.6e-15,0,0.100548)
  DirMode = 0
  FaceMakerClass = Part::FaceMakerBullseye
  LengthFwd = 0
  LengthRev = 0
  Solid = true
  Symmetric = false
FEATURE [Part::Cut] Cut038
  Base = -> Fusion013005002002
  Tool = -> Extrusion018
FEATURE [Part::Cut] Cut039
  Base = -> Cut038
  Tool = -> Extrusion017
FEATURE [Part::Cut] Cut040
  Base = -> Cut039
  Tool = -> Extrusion016
FEATURE [Part::Cut] Cut041
  Base = -> Cut040
  Tool = -> Extrusion015
FEATURE [Part::Cut] Cut042
  Base = -> Cut041
  Tool = -> Extrusion014
FEATURE [Part::Cut] Cut043
  Base = -> Cut042
  Tool = -> Extrusion013
FEATURE [Part::Cut] Cut044
  Base = -> Cut043
  Tool = -> Extrusion012
FEATURE [Part::Part2DObjectPython] Rectangle058  # Draft 2D object (typed FeaturePython)
  ChamferSize = 0
  Columns = 1
  FilletRadius = 0
  Height = 20.1
  Length = 3.8
  MakeFace = true
  Placement = pos=(-31.7381,33.4769,-0.534496) rot=(0.707107,0.707107,0;3.14159rad)
  Rows = 1
  Support = -> [Cut044]
FEATURE [Part::Extrusion] Extrude073
  Base = -> Rectangle058
  Dir = (2.5e-15,-2.5e-15,-1)
  DirMode = 2
  FaceMakerClass = Part::FaceMakerBullseye
  LengthFwd = -0.1
  LengthRev = 0
  Solid = false
  Symmetric = false
FEATURE [Part::Cut] Cut045
  Base = -> Cut044
  Tool = -> Extrude073
FEATURE [Part::Part2DObjectPython] Rectangle059  # Draft 2D object (typed FeaturePython)
  ChamferSize = 0
  Columns = 1
  FilletRadius = 0
  Height = 5.99945
  Length = 3.8
  MakeFace = true
  Placement = pos=(-11.6381,33.4769,-0.434496) rot=(0.57735,0.57735,0.57735;2.0944rad)
  Rows = 1
  Support = -> [Cut045]
FEATURE [Part::Extrusion] Extrude074
  Base = -> Rectangle059
  Dir = (1,0,0)
  DirMode = 2
  FaceMakerClass = Part::FaceMakerBullseye
  LengthFwd = -0.1
  LengthRev = 0
  Solid = false
  Symmetric = false
FEATURE [Part::Part2DObjectPython] Rectangle060  # Draft 2D object (typed FeaturePython)
  ChamferSize = 0
  Columns = 1
  FilletRadius = 0
  Height = 5.99945
  Length = 3.8
  MakeFace = true
  Placement = pos=(-31.7381,37.2769,-0.434496) rot=(0.57735,-0.57735,-0.57735;2.0944rad)
  Rows = 1
  Support = -> [Cut045]
FEATURE [Part::Extrusion] Extrude075
  Base = -> Rectangle060
  Dir = (-1,0,0)
  DirMode = 2
  FaceMakerClass = Part::FaceMakerBullseye
  LengthFwd = -0.1
  LengthRev = 0
  Solid = false
  Symmetric = false
FEATURE [Part::Cut] Cut046
  Base = -> Cut045
  Tool = -> Extrude075
FEATURE [Part::Cut] Cut047
  Base = -> Cut046
  Tool = -> Extrude074
FEATURE [Part::Feature] Cut047_solid  label="Cut047 (Solid)"
  shape: bbox 26 x 15.3 x 8.799 mm, 87 faces (baked)
FEATURE [Part::Feature] Cut047_solid001  label="Cut047 (Solid)001"
  Placement = pos=(36.0457,-1.82656,-3.1e-15) rot=(0,0,1;0rad)
  shape: bbox 26 x 15.3 x 8.799 mm, 30 faces (baked)
